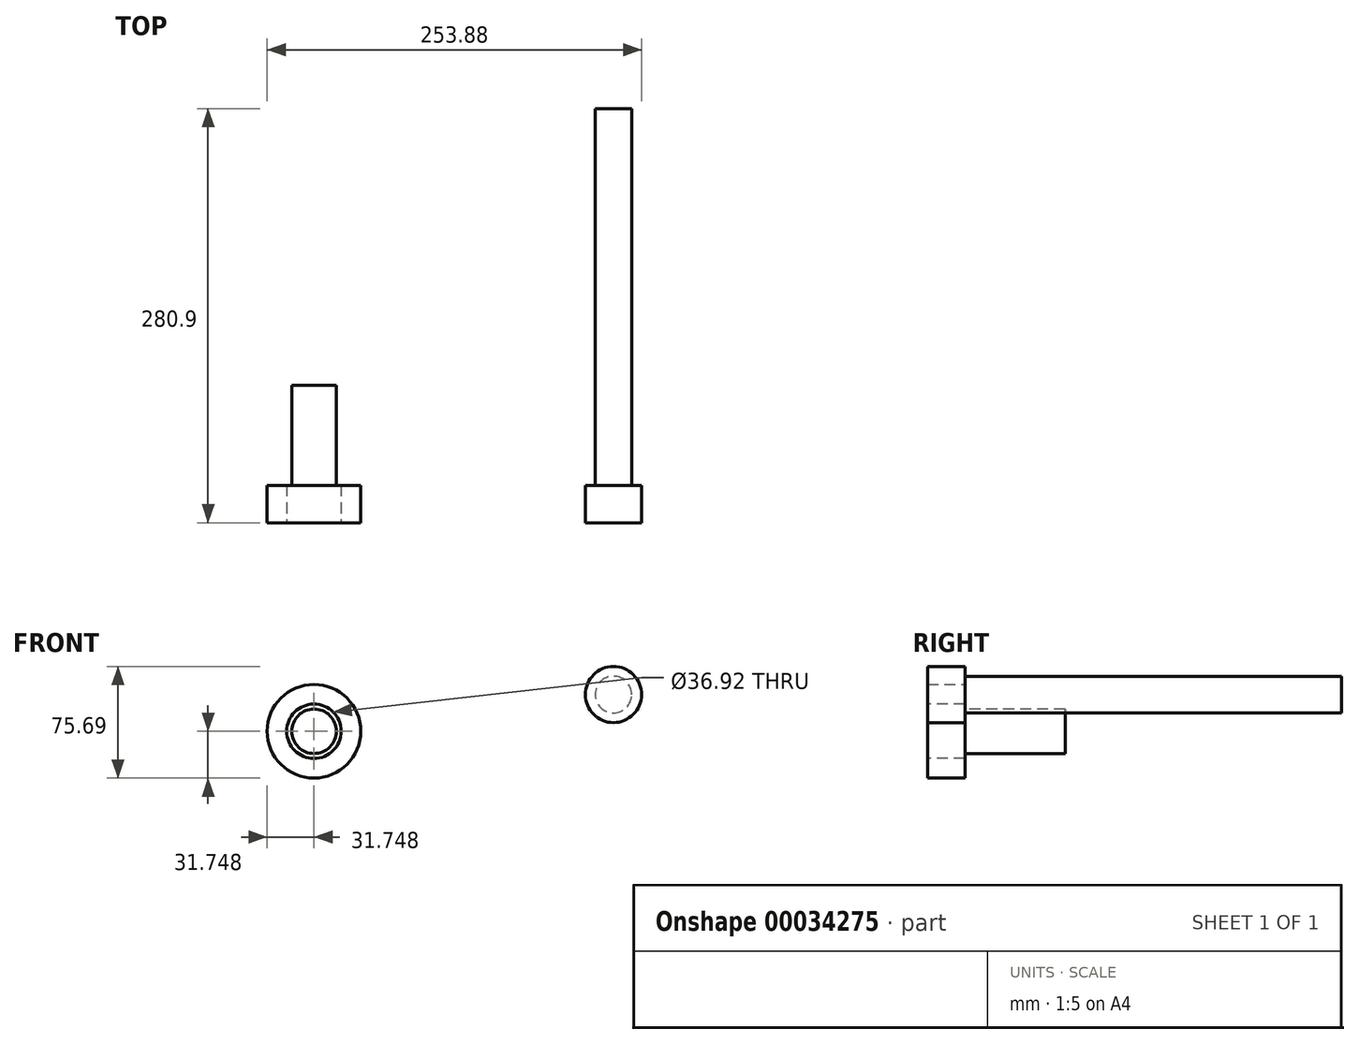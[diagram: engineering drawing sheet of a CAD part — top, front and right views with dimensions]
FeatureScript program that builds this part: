
annotation { "Feature Type Name" : "Feature", "Feature Type Description" : "" }
export const myFeature = defineFeature(function(context is Context, id is Id, definition is map)
    precondition{}
    {
        {
            var Q0;
            Q0=qCreatedBy(makeId("Front.planeOp"),FACE);
            var sketch = newSketch(context, id + "F0", { "sketchPlane" : qUnion([Q0])});
            skCircle(sketch, "E0", {"center": v(-106.97, -24.9) * mm, "radius": 31.75 * mm});
            skSolve(sketch);
        }
        {
            var Q0;
            Q0=makeQuery(id+"F0.imprint","IMPRINT",FACE,{"disambiguationData":[TD([[makeQuery(id+"F0.imprint","IMPRINT",EDGE,{"derivedFrom":sQuery(id+"F0.wireOp",EDGE,"E0")}),1.0]])]});
            extrude(context, id + "F1", {"entities" : qUnion([Q0]), "depth" : 25.4 * mm});
        }
        {
            var Q0;
            Q0=makeQuery(id+"F1.opExtrude","CAP_FACE",FACE,{"disambiguationData":[OSD([sQuery(id+"F0.wireOp",EDGE,"E0")])],"isStart":false});
            var sketch = newSketch(context, id + "F2", { "sketchPlane" : qUnion([Q0])});
            skCircle(sketch, "E1", {"center": v(-106.97, -24.9) * mm, "radius": 15.09 * mm});
            skSolve(sketch);
        }
        {
            var Q0;
            Q0=makeQuery(id+"F2.imprint","IMPRINT",FACE,{"disambiguationData":[TD([[makeQuery(id+"F2.imprint","IMPRINT",EDGE,{"derivedFrom":sQuery(id+"F2.wireOp",EDGE,"E1")}),1.0]])]});
            extrude(context, id + "F3", {"entities" : qUnion([Q0]), "operationType" : NewBodyOperationType.ADD, "endBound" : BoundingType.THROUGH_ALL, "oppositeDirection" : true, "depth" : 25.4 * mm});
        }
        {
            var Q0;
            Q0=qCreatedBy(makeId("Front.planeOp"),FACE);
            var sketch = newSketch(context, id + "F4", { "sketchPlane" : qUnion([Q0])});
            skCircle(sketch, "E2", {"center": v(96.11, 0) * mm, "radius": 19.05 * mm});
            skSolve(sketch);
        }
        {
            var Q0;
            Q0 = qSketchRegion(id + "F4", true);
            extrude(context, id + "F5", {"entities" : qUnion([Q0]), "depth" : 25.4 * mm});
        }
        {
            var Q0;
            Q0=makeQuery(id+"F5.opExtrude","CAP_FACE",FACE,{"disambiguationData":[OSD([sQuery(id+"F4.wireOp",EDGE,"E2")])],"isStart":false});
            var sketch = newSketch(context, id + "F6", { "sketchPlane" : qUnion([Q0])});
            skCircle(sketch, "E3", {"center": v(96.11, 0) * mm, "radius": 12.4 * mm});
            skSolve(sketch);
        }
        {
            var Q0;
            Q0 = qSketchRegion(id + "F6", true);
            extrude(context, id + "F7", {"entities" : qUnion([Q0]), "operationType" : NewBodyOperationType.ADD, "endBound" : BoundingType.THROUGH_ALL, "oppositeDirection" : true, "depth" : 25.4 * mm});
        }
        {
            var Q0;
            Q0=makeQuery(id+"F1.opExtrude","CAP_FACE",FACE,{"disambiguationData":[OSD([sQuery(id+"F0.wireOp",EDGE,"E0")])],"isStart":false});
            var sketch = newSketch(context, id + "F8", { "sketchPlane" : qUnion([Q0])});
            skCircle(sketch, "E4", {"center": v(-103.87, -24.51) * mm, "radius": 6.64 * mm});
            skSolve(sketch);
        }
        {
            var Q0;
            Q0 = qSketchRegion(id + "F8", true);
            extrude(context, id + "F9", {"entities" : qUnion([Q0]), "operationType" : NewBodyOperationType.ADD, "oppositeDirection" : true, "depth" : 25.4 * mm});
        }
        {
            var Q0;
            Q0=makeQuery(id+"F1.opExtrude","CAP_FACE",FACE,{"disambiguationData":[OSD([sQuery(id+"F0.wireOp",EDGE,"E0")])],"isStart":false});
            var sketch = newSketch(context, id + "F10", { "sketchPlane" : qUnion([Q0])});
            skCircle(sketch, "E5", {"center": v(-106.97, -24.9) * mm, "radius": 18.46 * mm});
            skSolve(sketch);
        }
        {
            var Q0;
            Q0=makeQuery(id+"F10.imprint","IMPRINT",FACE,{"disambiguationData":[TD([[makeQuery(id+"F10.imprint","IMPRINT",EDGE,{"derivedFrom":sQuery(id+"F10.wireOp",EDGE,"E5")}),1.0]])]});
            extrude(context, id + "F11", {"entities" : qUnion([Q0]), "operationType" : NewBodyOperationType.REMOVE, "oppositeDirection" : true, "depth" : 25.4 * mm});
        }
    });
